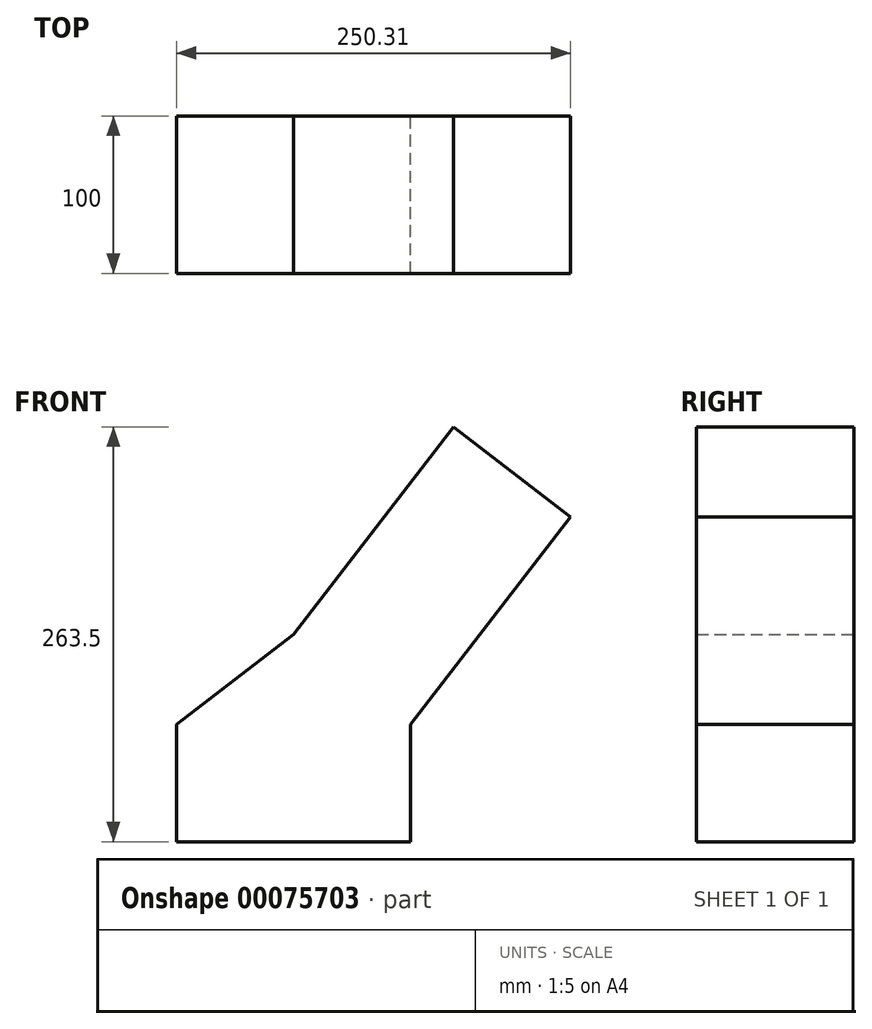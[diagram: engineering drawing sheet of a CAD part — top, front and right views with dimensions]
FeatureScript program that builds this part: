
annotation { "Feature Type Name" : "Feature", "Feature Type Description" : "" }
export const myFeature = defineFeature(function(context is Context, id is Id, definition is map)
    precondition{}
    {
        {
            var Q0;
            Q0=qCreatedBy(makeId("Front.planeOp"),FACE);
            var sketch = newSketch(context, id + "F0", { "sketchPlane" : qUnion([Q0])});
            skLineSegment(sketch, "E0.bottom", {"start": v(-74.3, 0) * mm, "end": v(74.3, 0) * mm});
            skLineSegment(sketch, "E0.top", {"start": v(-74.3, -74.3) * mm, "end": v(74.3, -74.3) * mm});
            skLineSegment(sketch, "E0.left", {"start": v(-74.3, 0) * mm, "end": v(-74.3, -74.3) * mm});
            skLineSegment(sketch, "E0.right", {"start": v(74.3, 0) * mm, "end": v(74.3, -74.3) * mm});
            skLineSegment(sketch, "E1", {"start": v(-74.3, 0) * mm, "end": v(0, 57.28) * mm});
            skLineSegment(sketch, "E2", {"start": v(0, 57.28) * mm, "end": v(74.3, 0) * mm});
            skSolve(sketch);
        }
        {
            var Q0;
            Q0=makeQuery(id+"F0.imprint","IMPRINT",FACE,{"disambiguationData":[TD([[makeQuery(id+"F0.imprint","IMPRINT",EDGE,{"derivedFrom":sQuery(id+"F0.wireOp",EDGE,"E0.bottom")}),1.0]])]});
            var Q1;
            Q1=makeQuery(id+"F0.imprint","IMPRINT",FACE,{"disambiguationData":[TD([[makeQuery(id+"F0.imprint","IMPRINT",EDGE,{"derivedFrom":sQuery(id+"F0.wireOp",EDGE,"E0.bottom")}),-1.0]])]});
            extrude(context, id + "F1", {"entities" : qUnion([Q0, Q1]), "depth" : 100 * mm});
        }
        {
            var Q0;
            Q0=makeQuery(id+"F1.opExtrude","SWEPT_FACE",FACE,{"disambiguationData":[OSD([sQuery(id+"F0.wireOp",EDGE,"E2")])]});
            extrude(context, id + "F2", {"entities" : qUnion([Q0]), "operationType" : NewBodyOperationType.ADD, "depth" : 166.56 * mm});
        }
    });
